# Revit family: HVAC-Chilled_Beam-Dadanco-ACB45
name_source: partatom
category: Mechanical Equipment
revit_build: Autodesk Revit 2015 (Build: 20140903_1530(x64)
units: mm (PartAtom-declared; Revit-internal decimal feet)

## types (5) — shared parameters
0.5 inch Female NPT Stub coil Connection = No
0.5 inch Male NPT Stub Coil Connection = No
0.5 inch SWT Stub Coil Connection = Yes
2 Pipe Coil Configuration = Yes
2 or 4 pipe = 2
4 Pipe Coil Configuration = No
Architectural Design Manual = http://www.activechilledbeam.com
Assembly Code = D3040100
CWF = 0 GPM
CWPD = 0.00 ftH2O
Cooling Primary Air Dry Bulb = 0 °F
Cooling Primary Air Wet Bulb = 0 °F
Cooling Room Dry Bulb = 0 °F
Cooling Supply Air Temperature = 0 °F
Description = Active Chilled Beam
Documentation Link = http://www.dadanco.com
HWF = 0 GPM
HWPD = 0.00 ftH2O
Heating Primary Air Dry Bulb = 0 °F
Heating Room Dry Bulb = 0 °F
Heating Supply Air Temperature = 0 °F
Housing Material = Metal-Dadanco-Steel-Galvanized
Keynote = 23 37 00.A1
Latent Cooling = 0.0 Btu/h
Manufacturer = Dadanco
Model = ACB40
Net Unit Cooling Sensible = 0.0 Btu/h
Net Unit Heating Sensible = 0.0 Btu/h
PA = 0 CFM
PASP = 0.00 in-wg
Pipe Coil Inlet = 2 Pipe Coi, 0.5 inch SWT Stub Coil Connection
Pipe Coil Outlet = 2 Pipe Coi, 0.5 inch SWT Stub Coil Connection
Pipe Material = Metal-Dadanco-Copper-Satin
Primary Air Inlet Size = 0' - 6"
Product Page URL = http://www.activechilledbeam.com
Revision Date = 07/19/2010
SCHW Temp Out = 0 °F
SCHW Temperature = 0 °F
SHHW Temp Out = 0 °F
SHHW Temperature = 0 °F
Secondary Air Sensible Cooling = 0.0 Btu/h
Secondary Air Sensible Heating = 0.0 Btu/h
Supply Air = 0 CFM
Total Cooling Capacity = 0.0 Btu/h
Type Comments = 2-way Discharge Horizontal Coil
URL = http://www.dadanco.com
Unit Height = 0' - 11 3/32"
Unit Width = 1' - 11 3/4"
zero-valued in all types: Cooling Room Relative Humidity

## per-type parameters (varying)
| type | Center Bracket | Coil Length | Nominal Unit Length | Origin1 | Overall Unit Length | Unit Length | Weight |
| 4' Nominal Length | No | 3' - 4" | 4' - 0" | 2' - 0" | 4' - 2 1/2" | 3' - 11 3/4" | 70 lb |
| 2' Nominal Length | No | 2' - 0" | 2' - 0" | 1' - 0" | 2' - 2 1/2" | 1' - 11 3/4" | 40 lb |
| 6' Nominal Length | No | 5' - 4" | 6' - 0" | 3' - 0" | 6' - 2 1/2" | 5' - 11 3/4" | 110 lb |
| 8' Nominal Length | Yes | 0' - 0" | 8' - 0" | 4' - 0" | 8' - 2 1/2" | 7' - 11 3/4" | 0 lb |
| 10' Nominal Length | Yes | 0' - 0" | 10' - 0" | 5' - 0" | 10' - 2 1/2" | 9' - 11 3/4" | 0 lb |

## geometry (parser evidence)
native form markers: Sweep x1
no freeform markers — native parametric forms only
